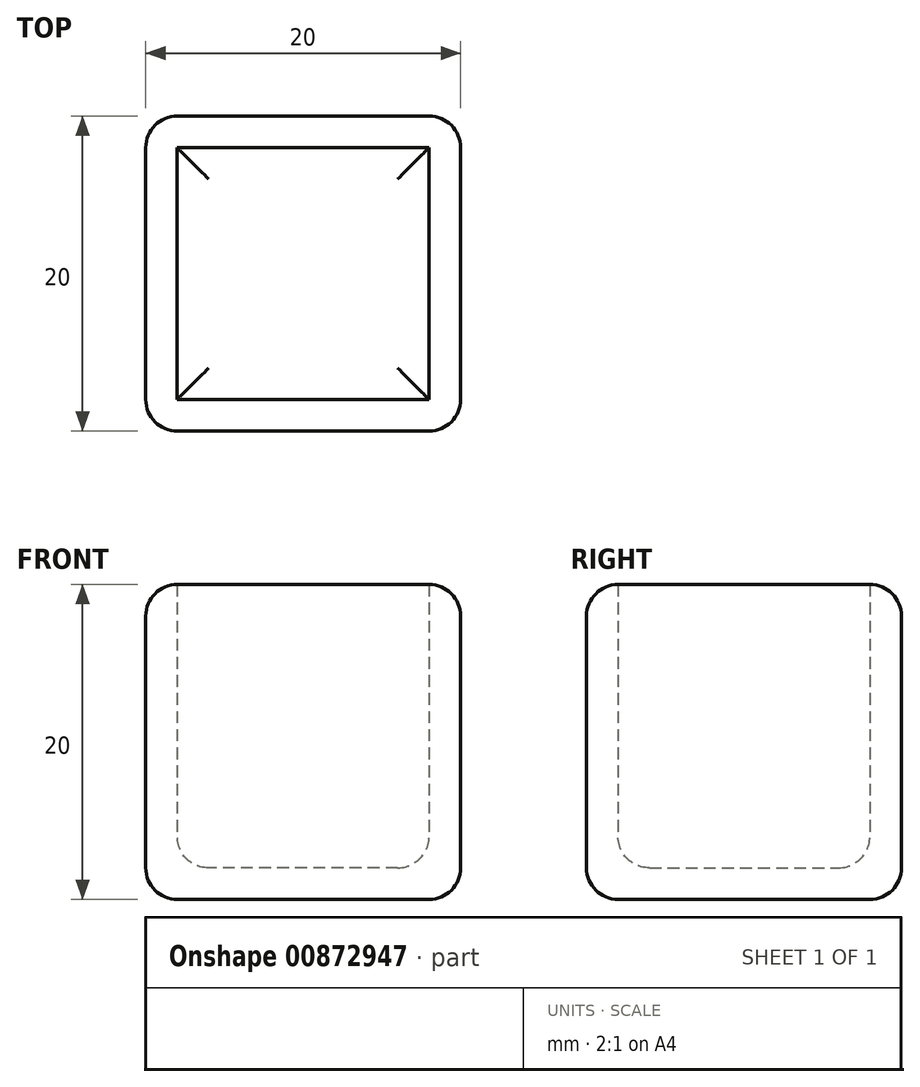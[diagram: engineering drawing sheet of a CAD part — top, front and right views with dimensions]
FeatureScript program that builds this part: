
annotation { "Feature Type Name" : "Feature", "Feature Type Description" : "" }
export const myFeature = defineFeature(function(context is Context, id is Id, definition is map)
    precondition{}
    {
        {
            var Q0;
            Q0=qCreatedBy(makeId("Top.planeOp"),FACE);
            var sketch = newSketch(context, id + "F0", { "sketchPlane" : qUnion([Q0])});
            skLineSegment(sketch, "E0.bottom", {"start": v(8, -10) * mm, "end": v(-8, -10) * mm});
            skLineSegment(sketch, "E0.top", {"start": v(8, 10) * mm, "end": v(-8, 10) * mm});
            skLineSegment(sketch, "E0.left", {"start": v(10, -8) * mm, "end": v(10, 8) * mm});
            skLineSegment(sketch, "E0.right", {"start": v(-10, -8) * mm, "end": v(-10, 8) * mm});
            skPoint(sketch, "E0.middle", {"position": v(0, 0) * mm});
            skPoint(sketch, "E1.visualSharp", {"position": v(-10, 10) * mm});
            skArc(sketch, "E1.filletArc", {"start": v(-8, 10) * mm, "mid": v(-9.41, 9.41) * mm, "end": v(-10, 8) * mm});
            skPoint(sketch, "E2.visualSharp", {"position": v(10, 10) * mm});
            skArc(sketch, "E2.filletArc", {"start": v(10, 8) * mm, "mid": v(9.41, 9.41) * mm, "end": v(8, 10) * mm});
            skPoint(sketch, "E3.visualSharp", {"position": v(10, -10) * mm});
            skArc(sketch, "E3.filletArc", {"start": v(8, -10) * mm, "mid": v(9.41, -9.41) * mm, "end": v(10, -8) * mm});
            skPoint(sketch, "E4.visualSharp", {"position": v(-10, -10) * mm});
            skArc(sketch, "E4.filletArc", {"start": v(-10, -8) * mm, "mid": v(-9.41, -9.41) * mm, "end": v(-8, -10) * mm});
            skSolve(sketch);
        }
        {
            var Q0;
            Q0=makeQuery(id+"F0.imprint","IMPRINT",FACE,{"disambiguationData":[TD([[makeQuery(id+"F0.imprint","IMPRINT",EDGE,{"derivedFrom":sQuery(id+"F0.wireOp",EDGE,"E0.bottom")}),-1.0]])]});
            extrude(context, id + "F1", {"entities" : qUnion([Q0]), "depth" : 20 * mm, "offsetDistance" : 25 * mm});
        }
        {
            var Q0;
            Q0=makeQuery(id+"F1.opExtrude","CAP_FACE",FACE,{"disambiguationData":[OSD([sQuery(id+"F0.wireOp",EDGE,"E0.bottom"),sQuery(id+"F0.wireOp",EDGE,"E0.top"),sQuery(id+"F0.wireOp",EDGE,"E0.left"),sQuery(id+"F0.wireOp",EDGE,"E0.right"),sQuery(id+"F0.wireOp",EDGE,"E1.filletArc"),sQuery(id+"F0.wireOp",EDGE,"E2.filletArc"),sQuery(id+"F0.wireOp",EDGE,"E3.filletArc"),sQuery(id+"F0.wireOp",EDGE,"E4.filletArc")])],"isStart":false});
            var Q1;
            Q1=makeQuery(id+"F1.opExtrude","CAP_FACE",FACE,{"disambiguationData":[OSD([sQuery(id+"F0.wireOp",EDGE,"E0.bottom"),sQuery(id+"F0.wireOp",EDGE,"E0.top"),sQuery(id+"F0.wireOp",EDGE,"E0.left"),sQuery(id+"F0.wireOp",EDGE,"E0.right"),sQuery(id+"F0.wireOp",EDGE,"E1.filletArc"),sQuery(id+"F0.wireOp",EDGE,"E2.filletArc"),sQuery(id+"F0.wireOp",EDGE,"E3.filletArc"),sQuery(id+"F0.wireOp",EDGE,"E4.filletArc")])],"isStart":true});
            fillet(context, id + "F2", {"entities" : qUnion([Q0, Q1]), "radius" : 2 * mm, "tangentPropagation" : true, "allowEdgeOverflow" : false});
        }
        {
            var Q0;
            Q0=makeQuery(id+"F1.opExtrude","CAP_FACE",FACE,{"disambiguationData":[OSD([sQuery(id+"F0.wireOp",EDGE,"E0.bottom"),sQuery(id+"F0.wireOp",EDGE,"E0.top"),sQuery(id+"F0.wireOp",EDGE,"E0.left"),sQuery(id+"F0.wireOp",EDGE,"E0.right"),sQuery(id+"F0.wireOp",EDGE,"E1.filletArc"),sQuery(id+"F0.wireOp",EDGE,"E2.filletArc"),sQuery(id+"F0.wireOp",EDGE,"E3.filletArc"),sQuery(id+"F0.wireOp",EDGE,"E4.filletArc")])],"isStart":false});
            shell(context, id + "F3", {"entities" : qUnion([Q0]), "thickness" : 2 * mm});
        }
        {
            var Q0;
            {var subQ0=sQuery(id+"F0.wireOp",EDGE,"E0.top");var subQ1=makeQuery(id+"F1.opExtrude","CAP_EDGE",EDGE,{"disambiguationData":[OSD([subQ0])],"isStart":true});var subQ2=sQuery(id+"F0.wireOp",EDGE,"E4.filletArc");var subQ3=sQuery(id+"F0.wireOp",EDGE,"E3.filletArc");var subQ4=sQuery(id+"F0.wireOp",EDGE,"E2.filletArc");var subQ5=sQuery(id+"F0.wireOp",EDGE,"E1.filletArc");var subQ6=sQuery(id+"F0.wireOp",EDGE,"E0.right");var subQ7=sQuery(id+"F0.wireOp",EDGE,"E0.left");var subQ8=sQuery(id+"F0.wireOp",EDGE,"E0.bottom");Q0=makeQuery(id+"F3.opShell","OFFSET_EDGE",EDGE,{"disambiguationData":[OSD([subQ8,subQ0,subQ7,subQ6,subQ5,subQ4,subQ3,subQ2]),TDD([makeQuery(id+"F2.opFillet","BLEND_EDGE",EDGE,{"blendedFrom":[subQ1,makeQuery(id+"F1.opExtrude","CAP_FACE",FACE,{"disambiguationData":[OSD([subQ8,subQ0,subQ7,subQ6,subQ5,subQ4,subQ3,subQ2])],"isStart":true})],"blendedInto":[makeQuery(id+"F1.opExtrude","CAP_FACE",FACE,{"disambiguationData":[OSD([subQ8,subQ0,subQ7,subQ6,subQ5,subQ4,subQ3,subQ2])],"isStart":true})]}),makeQuery(id+"F2.opFillet","BLEND_EDGE",EDGE,{"blendedFrom":[subQ1,makeQuery(id+"F1.opExtrude","SWEPT_FACE",FACE,{"disambiguationData":[OSD([subQ0])]})],"blendedInto":[makeQuery(id+"F1.opExtrude","SWEPT_FACE",FACE,{"disambiguationData":[OSD([subQ0])]})]})])]});}
            var Q1;
            {var subQ0=sQuery(id+"F0.wireOp",EDGE,"E0.right");var subQ1=makeQuery(id+"F1.opExtrude","CAP_EDGE",EDGE,{"disambiguationData":[OSD([subQ0])],"isStart":true});var subQ2=sQuery(id+"F0.wireOp",EDGE,"E4.filletArc");var subQ3=sQuery(id+"F0.wireOp",EDGE,"E3.filletArc");var subQ4=sQuery(id+"F0.wireOp",EDGE,"E2.filletArc");var subQ5=sQuery(id+"F0.wireOp",EDGE,"E1.filletArc");var subQ6=sQuery(id+"F0.wireOp",EDGE,"E0.left");var subQ7=sQuery(id+"F0.wireOp",EDGE,"E0.top");var subQ8=sQuery(id+"F0.wireOp",EDGE,"E0.bottom");Q1=makeQuery(id+"F3.opShell","OFFSET_EDGE",EDGE,{"disambiguationData":[OSD([subQ8,subQ7,subQ6,subQ0,subQ5,subQ4,subQ3,subQ2]),TDD([makeQuery(id+"F2.opFillet","BLEND_EDGE",EDGE,{"blendedFrom":[subQ1,makeQuery(id+"F1.opExtrude","CAP_FACE",FACE,{"disambiguationData":[OSD([subQ8,subQ7,subQ6,subQ0,subQ5,subQ4,subQ3,subQ2])],"isStart":true})],"blendedInto":[makeQuery(id+"F1.opExtrude","CAP_FACE",FACE,{"disambiguationData":[OSD([subQ8,subQ7,subQ6,subQ0,subQ5,subQ4,subQ3,subQ2])],"isStart":true})]}),makeQuery(id+"F2.opFillet","BLEND_EDGE",EDGE,{"blendedFrom":[subQ1,makeQuery(id+"F1.opExtrude","SWEPT_FACE",FACE,{"disambiguationData":[OSD([subQ0])]})],"blendedInto":[makeQuery(id+"F1.opExtrude","SWEPT_FACE",FACE,{"disambiguationData":[OSD([subQ0])]})]})])]});}
            var Q2;
            {var subQ0=sQuery(id+"F0.wireOp",EDGE,"E4.filletArc");var subQ1=sQuery(id+"F0.wireOp",EDGE,"E3.filletArc");var subQ2=sQuery(id+"F0.wireOp",EDGE,"E2.filletArc");var subQ3=sQuery(id+"F0.wireOp",EDGE,"E1.filletArc");var subQ4=sQuery(id+"F0.wireOp",EDGE,"E0.right");var subQ5=sQuery(id+"F0.wireOp",EDGE,"E0.left");var subQ6=sQuery(id+"F0.wireOp",EDGE,"E0.top");var subQ7=sQuery(id+"F0.wireOp",EDGE,"E0.bottom");var subQ8=makeQuery(id+"F1.opExtrude","CAP_EDGE",EDGE,{"disambiguationData":[OSD([subQ7])],"isStart":true});Q2=makeQuery(id+"F3.opShell","OFFSET_EDGE",EDGE,{"disambiguationData":[OSD([subQ7,subQ6,subQ5,subQ4,subQ3,subQ2,subQ1,subQ0]),TDD([makeQuery(id+"F2.opFillet","BLEND_EDGE",EDGE,{"blendedFrom":[subQ8,makeQuery(id+"F1.opExtrude","SWEPT_FACE",FACE,{"disambiguationData":[OSD([subQ7])]})],"blendedInto":[makeQuery(id+"F1.opExtrude","SWEPT_FACE",FACE,{"disambiguationData":[OSD([subQ7])]})]}),makeQuery(id+"F2.opFillet","BLEND_EDGE",EDGE,{"blendedFrom":[subQ8,makeQuery(id+"F1.opExtrude","CAP_FACE",FACE,{"disambiguationData":[OSD([subQ7,subQ6,subQ5,subQ4,subQ3,subQ2,subQ1,subQ0])],"isStart":true})],"blendedInto":[makeQuery(id+"F1.opExtrude","CAP_FACE",FACE,{"disambiguationData":[OSD([subQ7,subQ6,subQ5,subQ4,subQ3,subQ2,subQ1,subQ0])],"isStart":true})]})])]});}
            var Q3;
            {var subQ0=sQuery(id+"F0.wireOp",EDGE,"E0.left");var subQ1=makeQuery(id+"F1.opExtrude","CAP_EDGE",EDGE,{"disambiguationData":[OSD([subQ0])],"isStart":true});var subQ2=sQuery(id+"F0.wireOp",EDGE,"E4.filletArc");var subQ3=sQuery(id+"F0.wireOp",EDGE,"E3.filletArc");var subQ4=sQuery(id+"F0.wireOp",EDGE,"E2.filletArc");var subQ5=sQuery(id+"F0.wireOp",EDGE,"E1.filletArc");var subQ6=sQuery(id+"F0.wireOp",EDGE,"E0.right");var subQ7=sQuery(id+"F0.wireOp",EDGE,"E0.top");var subQ8=sQuery(id+"F0.wireOp",EDGE,"E0.bottom");Q3=makeQuery(id+"F3.opShell","OFFSET_EDGE",EDGE,{"disambiguationData":[OSD([subQ8,subQ7,subQ0,subQ6,subQ5,subQ4,subQ3,subQ2]),TDD([makeQuery(id+"F2.opFillet","BLEND_EDGE",EDGE,{"blendedFrom":[subQ1,makeQuery(id+"F1.opExtrude","CAP_FACE",FACE,{"disambiguationData":[OSD([subQ8,subQ7,subQ0,subQ6,subQ5,subQ4,subQ3,subQ2])],"isStart":true})],"blendedInto":[makeQuery(id+"F1.opExtrude","CAP_FACE",FACE,{"disambiguationData":[OSD([subQ8,subQ7,subQ0,subQ6,subQ5,subQ4,subQ3,subQ2])],"isStart":true})]}),makeQuery(id+"F2.opFillet","BLEND_EDGE",EDGE,{"blendedFrom":[subQ1,makeQuery(id+"F1.opExtrude","SWEPT_FACE",FACE,{"disambiguationData":[OSD([subQ0])]})],"blendedInto":[makeQuery(id+"F1.opExtrude","SWEPT_FACE",FACE,{"disambiguationData":[OSD([subQ0])]})]})])]});}
            fillet(context, id + "F4", {"entities" : qUnion([Q0, Q1, Q2, Q3]), "radius" : 2 * mm, "tangentPropagation" : true, "allowEdgeOverflow" : false});
        }
    });
